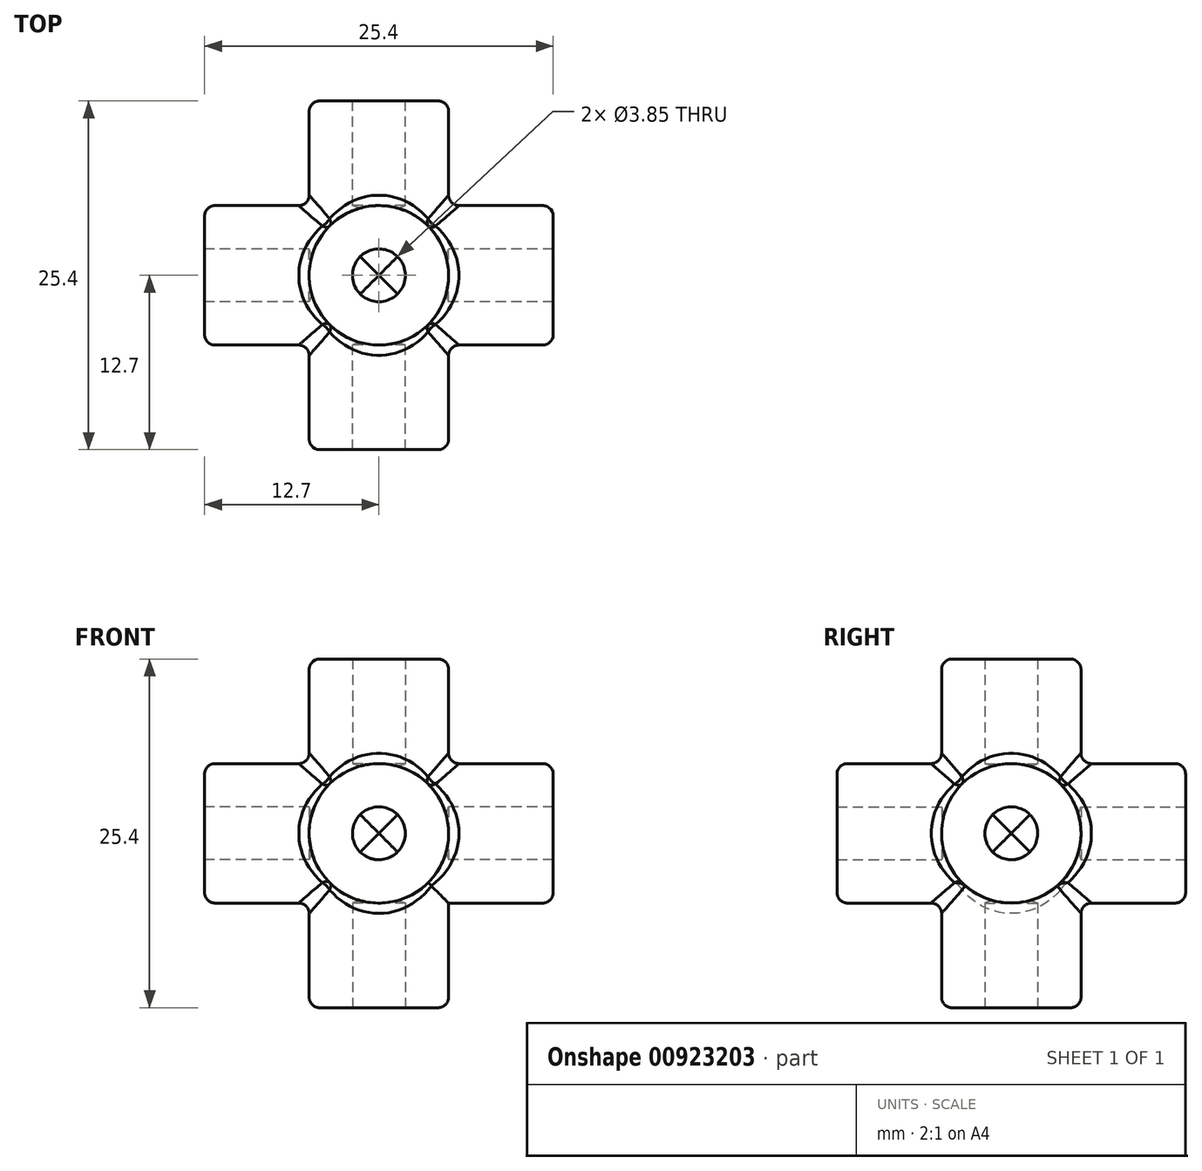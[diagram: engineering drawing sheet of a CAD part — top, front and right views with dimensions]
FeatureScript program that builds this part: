
annotation { "Feature Type Name" : "Feature", "Feature Type Description" : "" }
export const myFeature = defineFeature(function(context is Context, id is Id, definition is map)
    precondition{}
    {
        {
            var Q0;
            Q0=qCreatedBy(makeId("Front.planeOp"),FACE);
            var sketch = newSketch(context, id + "F0", { "sketchPlane" : qUnion([Q0])});
            skCircle(sketch, "E0", {"center": v(0, 0) * mm, "radius": 5.08 * mm});
            skCircle(sketch, "E1", {"center": v(0, 0) * mm, "radius": 1.92 * mm});
            skSolve(sketch);
        }
        {
            var Q0;
            Q0=makeQuery(id+"F0.imprint","IMPRINT",FACE,{"disambiguationData":[TD([[makeQuery(id+"F0.imprint","IMPRINT",EDGE,{"derivedFrom":sQuery(id+"F0.wireOp",EDGE,"E0")}),1.0]])]});
            extrude(context, id + "F1", {"entities" : qUnion([Q0]), "endBound" : BoundingType.SYMMETRIC, "depth" : 25.4 * mm, "offsetDistance" : 25.4 * mm});
        }
        {
            var Q0;
            Q0=qCreatedBy(makeId("Right.planeOp"),FACE);
            var sketch = newSketch(context, id + "F2", { "sketchPlane" : qUnion([Q0])});
            skCircle(sketch, "E2", {"center": v(0, 0) * mm, "radius": 1.92 * mm});
            skCircle(sketch, "E3", {"center": v(0, 0) * mm, "radius": 5.08 * mm});
            skSolve(sketch);
        }
        {
            var Q0;
            Q0=qCreatedBy(makeId("Top.planeOp"),FACE);
            var sketch = newSketch(context, id + "F3", { "sketchPlane" : qUnion([Q0])});
            skCircle(sketch, "E4", {"center": v(0, 0) * mm, "radius": 1.92 * mm});
            skCircle(sketch, "E5", {"center": v(0, 0) * mm, "radius": 5.08 * mm});
            skSolve(sketch);
        }
        {
            var Q0;
            Q0 = qSketchRegion(id + "F2", true);
            extrude(context, id + "F4", {"entities" : qUnion([Q0]), "operationType" : NewBodyOperationType.ADD, "endBound" : BoundingType.SYMMETRIC, "depth" : 25.4 * mm, "offsetDistance" : 25.4 * mm});
        }
        {
            var Q0;
            Q0=makeQuery(id+"F3.imprint","IMPRINT",FACE,{"disambiguationData":[TD([[makeQuery(id+"F3.imprint","IMPRINT",EDGE,{"derivedFrom":sQuery(id+"F3.wireOp",EDGE,"E4")}),-1.0]])]});
            extrude(context, id + "F5", {"entities" : qUnion([Q0]), "operationType" : NewBodyOperationType.ADD, "endBound" : BoundingType.SYMMETRIC, "depth" : 25.4 * mm, "offsetDistance" : 25.4 * mm});
        }
        {
            var Q0;
            Q0=makeQuery(id+"F5.opExtrude","CAP_EDGE",EDGE,{"disambiguationData":[OSD([sQuery(id+"F3.wireOp",EDGE,"E5")])],"isStart":false});
            var Q1;
            Q1=makeQuery(id+"F1.opExtrude","CAP_EDGE",EDGE,{"disambiguationData":[OSD([sQuery(id+"F0.wireOp",EDGE,"E0")])],"isStart":false});
            var Q2;
            Q2=makeQuery(id+"F4.opExtrude","CAP_EDGE",EDGE,{"disambiguationData":[OSD([sQuery(id+"F2.wireOp",EDGE,"E3")])],"isStart":false});
            var Q3;
            Q3=makeQuery(id+"F1.opExtrude","CAP_EDGE",EDGE,{"disambiguationData":[OSD([sQuery(id+"F0.wireOp",EDGE,"E0")])],"isStart":true});
            var Q4;
            Q4=makeQuery(id+"F5.opExtrude","CAP_EDGE",EDGE,{"disambiguationData":[OSD([sQuery(id+"F3.wireOp",EDGE,"E5")])],"isStart":true});
            var Q5;
            Q5=makeQuery(id+"F4.opExtrude","CAP_EDGE",EDGE,{"disambiguationData":[OSD([sQuery(id+"F2.wireOp",EDGE,"E3")])],"isStart":true});
            var Q6;
            {var subQ0=sQuery(id+"F0.wireOp",EDGE,"E0");var subQ1=makeQuery(id+"F1.opExtrude","SWEPT_FACE",FACE,{"disambiguationData":[OSD([subQ0])]});Q6=makeQuery(id+"F5.boolean.opBoolean","INTERSECT",EDGE,{"disambiguationData":[OD(0.0)],"derivedFrom":[makeQuery(id+"F4.boolean.opBoolean","SPLIT",FACE,{"disambiguationData":[TD([subQ1,makeQuery(id+"F1.opExtrude","CAP_FACE",FACE,{"disambiguationData":[OSD([subQ0,sQuery(id+"F0.wireOp",EDGE,"E1")])],"isStart":true}),makeQuery(id+"F4.opExtrude","SWEPT_FACE",FACE,{"disambiguationData":[OSD([sQuery(id+"F2.wireOp",EDGE,"E3")])]})])],"derivedFrom":subQ1}),makeQuery(id+"F5.opExtrude","SWEPT_FACE",FACE,{"disambiguationData":[OSD([sQuery(id+"F3.wireOp",EDGE,"E5")])]})]});}
            var Q7;
            {var subQ0=sQuery(id+"F2.wireOp",EDGE,"E3");var subQ1=makeQuery(id+"F4.opExtrude","SWEPT_FACE",FACE,{"disambiguationData":[OSD([subQ0])]});Q7=makeQuery(id+"F5.boolean.opBoolean","INTERSECT",EDGE,{"disambiguationData":[OD(0.0)],"derivedFrom":[makeQuery(id+"F4.boolean.opBoolean","SPLIT",FACE,{"disambiguationData":[TD([makeQuery(id+"F1.opExtrude","SWEPT_FACE",FACE,{"disambiguationData":[OSD([sQuery(id+"F0.wireOp",EDGE,"E0")])]}),makeQuery(id+"F4.opExtrude","CAP_FACE",FACE,{"disambiguationData":[OSD([sQuery(id+"F2.wireOp",EDGE,"E2"),subQ0])],"isStart":true}),subQ1])],"derivedFrom":subQ1}),makeQuery(id+"F5.opExtrude","SWEPT_FACE",FACE,{"disambiguationData":[OSD([sQuery(id+"F3.wireOp",EDGE,"E5")])]})]});}
            var Q8;
            {var subQ0=makeQuery(id+"F1.opExtrude","SWEPT_FACE",FACE,{"disambiguationData":[OSD([sQuery(id+"F0.wireOp",EDGE,"E0")])]});var subQ1=makeQuery(id+"F4.opExtrude","SWEPT_FACE",FACE,{"disambiguationData":[OSD([sQuery(id+"F2.wireOp",EDGE,"E3")])]});Q8=makeQuery(id+"F5.boolean.opBoolean","SPLIT",EDGE,{"disambiguationData":[TD([subQ0,subQ1,makeQuery(id+"F5.opExtrude","SWEPT_FACE",FACE,{"disambiguationData":[OSD([sQuery(id+"F3.wireOp",EDGE,"E5")])]})])],"derivedFrom":makeQuery(id+"F4.boolean.opBoolean","INTERSECT",EDGE,{"disambiguationData":[OD(0.0)],"derivedFrom":[subQ0,subQ1]})});}
            var Q9;
            {var subQ0=makeQuery(id+"F1.opExtrude","SWEPT_FACE",FACE,{"disambiguationData":[OSD([sQuery(id+"F0.wireOp",EDGE,"E0")])]});var subQ1=makeQuery(id+"F4.opExtrude","SWEPT_FACE",FACE,{"disambiguationData":[OSD([sQuery(id+"F2.wireOp",EDGE,"E3")])]});Q9=makeQuery(id+"F5.boolean.opBoolean","SPLIT",EDGE,{"disambiguationData":[TD([subQ0,subQ1,makeQuery(id+"F5.opExtrude","SWEPT_FACE",FACE,{"disambiguationData":[OSD([sQuery(id+"F3.wireOp",EDGE,"E5")])]})])],"derivedFrom":makeQuery(id+"F4.boolean.opBoolean","INTERSECT",EDGE,{"disambiguationData":[OD(2.0)],"derivedFrom":[subQ0,subQ1]})});}
            var Q10;
            {var subQ0=sQuery(id+"F0.wireOp",EDGE,"E0");var subQ1=makeQuery(id+"F1.opExtrude","SWEPT_FACE",FACE,{"disambiguationData":[OSD([subQ0])]});Q10=makeQuery(id+"F5.boolean.opBoolean","INTERSECT",EDGE,{"disambiguationData":[OD(0.0)],"derivedFrom":[makeQuery(id+"F4.boolean.opBoolean","SPLIT",FACE,{"disambiguationData":[TD([subQ1,makeQuery(id+"F1.opExtrude","CAP_FACE",FACE,{"disambiguationData":[OSD([subQ0,sQuery(id+"F0.wireOp",EDGE,"E1")])],"isStart":false}),makeQuery(id+"F4.opExtrude","SWEPT_FACE",FACE,{"disambiguationData":[OSD([sQuery(id+"F2.wireOp",EDGE,"E3")])]})])],"derivedFrom":subQ1}),makeQuery(id+"F5.opExtrude","SWEPT_FACE",FACE,{"disambiguationData":[OSD([sQuery(id+"F3.wireOp",EDGE,"E5")])]})]});}
            var Q11;
            {var subQ0=sQuery(id+"F0.wireOp",EDGE,"E0");var subQ1=makeQuery(id+"F1.opExtrude","SWEPT_FACE",FACE,{"disambiguationData":[OSD([subQ0])]});Q11=makeQuery(id+"F5.boolean.opBoolean","INTERSECT",EDGE,{"disambiguationData":[OD(1.0)],"derivedFrom":[makeQuery(id+"F4.boolean.opBoolean","SPLIT",FACE,{"disambiguationData":[TD([subQ1,makeQuery(id+"F1.opExtrude","CAP_FACE",FACE,{"disambiguationData":[OSD([subQ0,sQuery(id+"F0.wireOp",EDGE,"E1")])],"isStart":false}),makeQuery(id+"F4.opExtrude","SWEPT_FACE",FACE,{"disambiguationData":[OSD([sQuery(id+"F2.wireOp",EDGE,"E3")])]})])],"derivedFrom":subQ1}),makeQuery(id+"F5.opExtrude","SWEPT_FACE",FACE,{"disambiguationData":[OSD([sQuery(id+"F3.wireOp",EDGE,"E5")])]})]});}
            var Q12;
            {var subQ0=makeQuery(id+"F1.opExtrude","SWEPT_FACE",FACE,{"disambiguationData":[OSD([sQuery(id+"F0.wireOp",EDGE,"E0")])]});var subQ1=makeQuery(id+"F4.opExtrude","SWEPT_FACE",FACE,{"disambiguationData":[OSD([sQuery(id+"F2.wireOp",EDGE,"E3")])]});Q12=makeQuery(id+"F5.boolean.opBoolean","SPLIT",EDGE,{"disambiguationData":[TD([subQ0,subQ1,makeQuery(id+"F5.opExtrude","SWEPT_FACE",FACE,{"disambiguationData":[OSD([sQuery(id+"F3.wireOp",EDGE,"E5")])]})])],"derivedFrom":makeQuery(id+"F4.boolean.opBoolean","INTERSECT",EDGE,{"disambiguationData":[OD(3.0)],"derivedFrom":[subQ0,subQ1]})});}
            var Q13;
            {var subQ0=sQuery(id+"F2.wireOp",EDGE,"E3");var subQ1=makeQuery(id+"F4.opExtrude","SWEPT_FACE",FACE,{"disambiguationData":[OSD([subQ0])]});Q13=makeQuery(id+"F5.boolean.opBoolean","INTERSECT",EDGE,{"disambiguationData":[OD(1.0)],"derivedFrom":[makeQuery(id+"F4.boolean.opBoolean","SPLIT",FACE,{"disambiguationData":[TD([makeQuery(id+"F1.opExtrude","SWEPT_FACE",FACE,{"disambiguationData":[OSD([sQuery(id+"F0.wireOp",EDGE,"E0")])]}),makeQuery(id+"F4.opExtrude","CAP_FACE",FACE,{"disambiguationData":[OSD([sQuery(id+"F2.wireOp",EDGE,"E2"),subQ0])],"isStart":false}),subQ1])],"derivedFrom":subQ1}),makeQuery(id+"F5.opExtrude","SWEPT_FACE",FACE,{"disambiguationData":[OSD([sQuery(id+"F3.wireOp",EDGE,"E5")])]})]});}
            var Q14;
            {var subQ0=makeQuery(id+"F1.opExtrude","SWEPT_FACE",FACE,{"disambiguationData":[OSD([sQuery(id+"F0.wireOp",EDGE,"E0")])]});var subQ1=makeQuery(id+"F4.opExtrude","SWEPT_FACE",FACE,{"disambiguationData":[OSD([sQuery(id+"F2.wireOp",EDGE,"E3")])]});Q14=makeQuery(id+"F5.boolean.opBoolean","SPLIT",EDGE,{"disambiguationData":[TD([subQ0,subQ1,makeQuery(id+"F5.opExtrude","SWEPT_FACE",FACE,{"disambiguationData":[OSD([sQuery(id+"F3.wireOp",EDGE,"E5")])]})])],"derivedFrom":makeQuery(id+"F4.boolean.opBoolean","INTERSECT",EDGE,{"disambiguationData":[OD(1.0)],"derivedFrom":[subQ0,subQ1]})});}
            var Q15;
            {var subQ0=sQuery(id+"F0.wireOp",EDGE,"E0");var subQ1=makeQuery(id+"F1.opExtrude","SWEPT_FACE",FACE,{"disambiguationData":[OSD([subQ0])]});Q15=makeQuery(id+"F5.boolean.opBoolean","INTERSECT",EDGE,{"disambiguationData":[OD(1.0)],"derivedFrom":[makeQuery(id+"F4.boolean.opBoolean","SPLIT",FACE,{"disambiguationData":[TD([subQ1,makeQuery(id+"F1.opExtrude","CAP_FACE",FACE,{"disambiguationData":[OSD([subQ0,sQuery(id+"F0.wireOp",EDGE,"E1")])],"isStart":true}),makeQuery(id+"F4.opExtrude","SWEPT_FACE",FACE,{"disambiguationData":[OSD([sQuery(id+"F2.wireOp",EDGE,"E3")])]})])],"derivedFrom":subQ1}),makeQuery(id+"F5.opExtrude","SWEPT_FACE",FACE,{"disambiguationData":[OSD([sQuery(id+"F3.wireOp",EDGE,"E5")])]})]});}
            var Q16;
            {var subQ0=sQuery(id+"F2.wireOp",EDGE,"E3");var subQ1=makeQuery(id+"F4.opExtrude","SWEPT_FACE",FACE,{"disambiguationData":[OSD([subQ0])]});Q16=makeQuery(id+"F5.boolean.opBoolean","INTERSECT",EDGE,{"disambiguationData":[OD(1.0)],"derivedFrom":[makeQuery(id+"F4.boolean.opBoolean","SPLIT",FACE,{"disambiguationData":[TD([makeQuery(id+"F1.opExtrude","SWEPT_FACE",FACE,{"disambiguationData":[OSD([sQuery(id+"F0.wireOp",EDGE,"E0")])]}),makeQuery(id+"F4.opExtrude","CAP_FACE",FACE,{"disambiguationData":[OSD([sQuery(id+"F2.wireOp",EDGE,"E2"),subQ0])],"isStart":true}),subQ1])],"derivedFrom":subQ1}),makeQuery(id+"F5.opExtrude","SWEPT_FACE",FACE,{"disambiguationData":[OSD([sQuery(id+"F3.wireOp",EDGE,"E5")])]})]});}
            fillet(context, id + "F6", {"entities" : qUnion([Q0, Q1, Q2, Q3, Q4, Q5, Q6, Q7, Q8, Q9, Q10, Q11, Q12, Q13, Q14, Q15, Q16]), "radius" : 0.76 * mm, "tangentPropagation" : true, "allowEdgeOverflow" : false});
        }
    });
